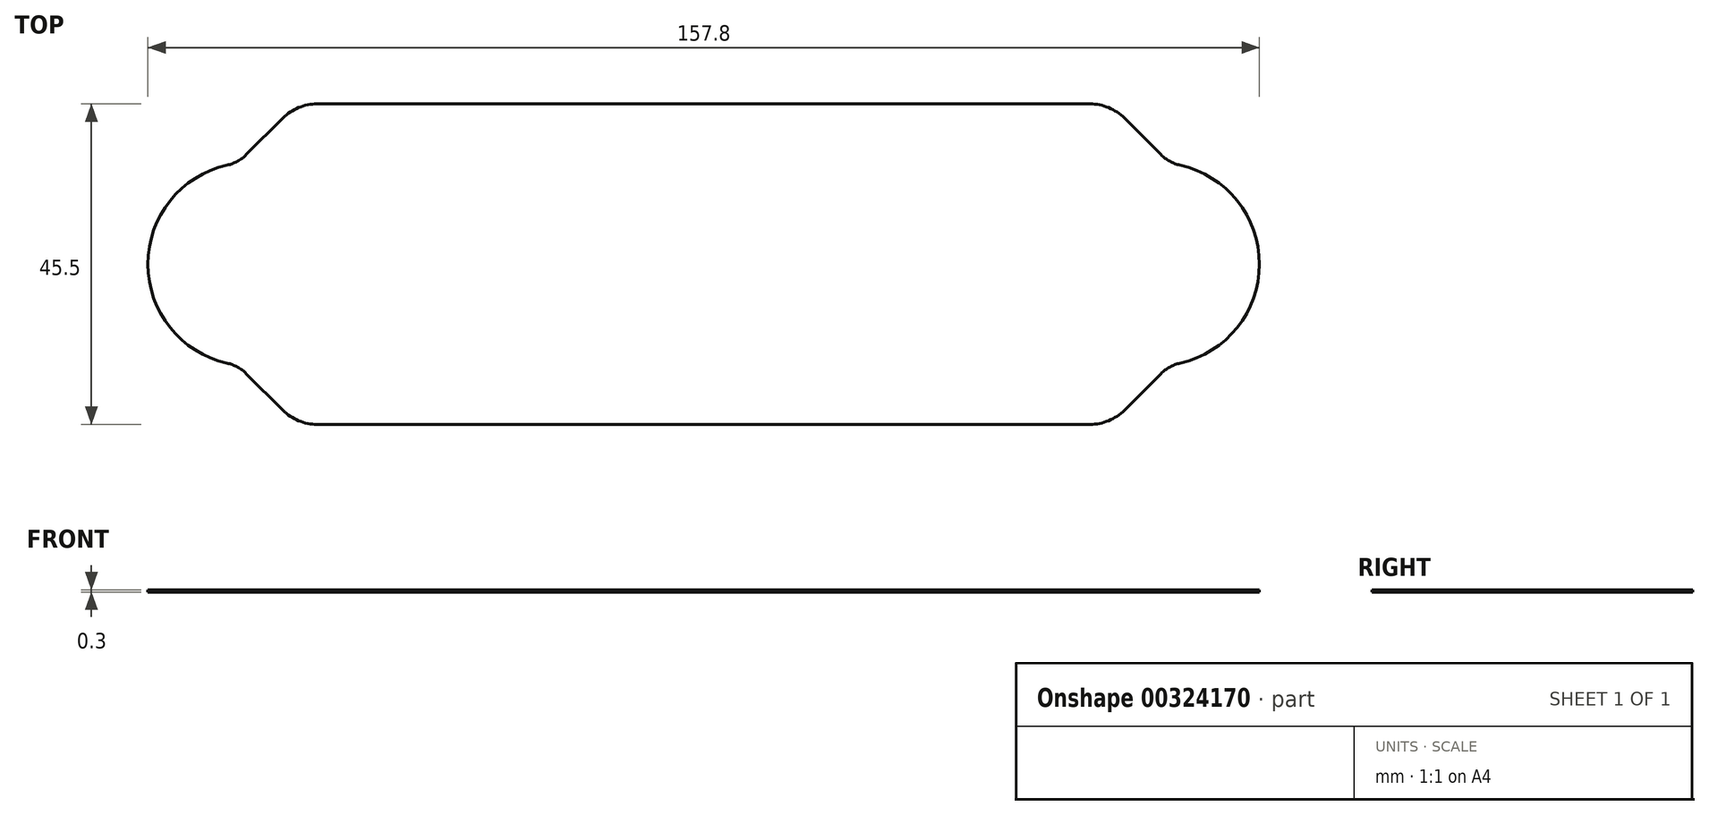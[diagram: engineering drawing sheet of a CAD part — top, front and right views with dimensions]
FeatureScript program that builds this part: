
annotation { "Feature Type Name" : "Feature", "Feature Type Description" : "" }
export const myFeature = defineFeature(function(context is Context, id is Id, definition is map)
    precondition{}
    {
        {
            var Q0;
            Q0=qCreatedBy(makeId("Top.planeOp"),FACE);
            var sketch = newSketch(context, id + "F0", { "sketchPlane" : qUnion([Q0])});
            skPoint(sketch, "E0", {"position": v(0, -3) * mm});
            skPoint(sketch, "E1.0.1.8", {"position": v(103.11, 3) * mm});
            skPoint(sketch, "E2.1.0.0", {"position": v(78.9, 0) * mm});
            skLineSegment(sketch, "E2.1.0.1", {"start": v(59.74, -20.73) * mm, "end": v(64.91, -15.56) * mm});
            skLineSegment(sketch, "E2.1.0.3", {"start": v(-54.86, 22.75) * mm, "end": v(54.86, 22.75) * mm});
            skArc(sketch, "E2.1.0.4", {"start": v(67.65, 14.06) * mm, "mid": v(78.9, 0) * mm, "end": v(67.65, -14.06) * mm});
            skLineSegment(sketch, "E2.1.0.6", {"start": v(59.74, 20.73) * mm, "end": v(64.91, 15.56) * mm});
            skArc(sketch, "E2.1.0.7", {"start": v(67.65, 14.06) * mm, "mid": v(66.17, 14.61) * mm, "end": v(64.91, 15.56) * mm});
            skArc(sketch, "E2.1.0.8", {"start": v(54.86, 22.75) * mm, "mid": v(57.5, 22.23) * mm, "end": v(59.74, 20.73) * mm});
            skArc(sketch, "E2.1.0.9", {"start": v(54.86, -22.75) * mm, "mid": v(57.5, -22.23) * mm, "end": v(59.74, -20.73) * mm});
            skArc(sketch, "E2.1.0.10", {"start": v(67.65, -14.06) * mm, "mid": v(66.17, -14.61) * mm, "end": v(64.91, -15.56) * mm});
            skLineSegment(sketch, "E3", {"start": v(0, -3) * mm, "end": v(0, 17.46) * mm});
            skArc(sketch, "E4.MirrorCS", {"start": v(-54.86, 22.75) * mm, "mid": v(-57.5, 22.23) * mm, "end": v(-59.74, 20.73) * mm});
            skArc(sketch, "E5.MirrorCS", {"start": v(-54.86, -22.75) * mm, "mid": v(-57.5, -22.23) * mm, "end": v(-59.74, -20.73) * mm});
            skLineSegment(sketch, "E6.MirrorCS", {"start": v(-59.74, -20.73) * mm, "end": v(-64.91, -15.56) * mm});
            skArc(sketch, "E7.MirrorCS", {"start": v(-67.65, 14.06) * mm, "mid": v(-78.9, 0) * mm, "end": v(-67.65, -14.06) * mm});
            skLineSegment(sketch, "E8.MirrorCS", {"start": v(-59.74, 20.73) * mm, "end": v(-64.91, 15.56) * mm});
            skArc(sketch, "E9.MirrorCS", {"start": v(-67.65, 14.06) * mm, "mid": v(-66.17, 14.61) * mm, "end": v(-64.91, 15.56) * mm});
            skArc(sketch, "E10.MirrorCS", {"start": v(-67.65, -14.06) * mm, "mid": v(-66.17, -14.61) * mm, "end": v(-64.91, -15.56) * mm});
            skLineSegment(sketch, "E11", {"start": v(-54.86, -22.75) * mm, "end": v(54.86, -22.75) * mm});
            skSolve(sketch);
        }
        {
            var Q0;
            Q0=makeQuery(id+"F0.imprint","IMPRINT",FACE,{"disambiguationData":[TD([[makeQuery(id+"F0.imprint","IMPRINT",EDGE,{"derivedFrom":sQuery(id+"F0.wireOp",EDGE,"E2.1.0.1")}),1.0]])]});
            extrude(context, id + "F1", {"entities" : qUnion([Q0]), "depth" : 0.3 * mm});
        }
    });
